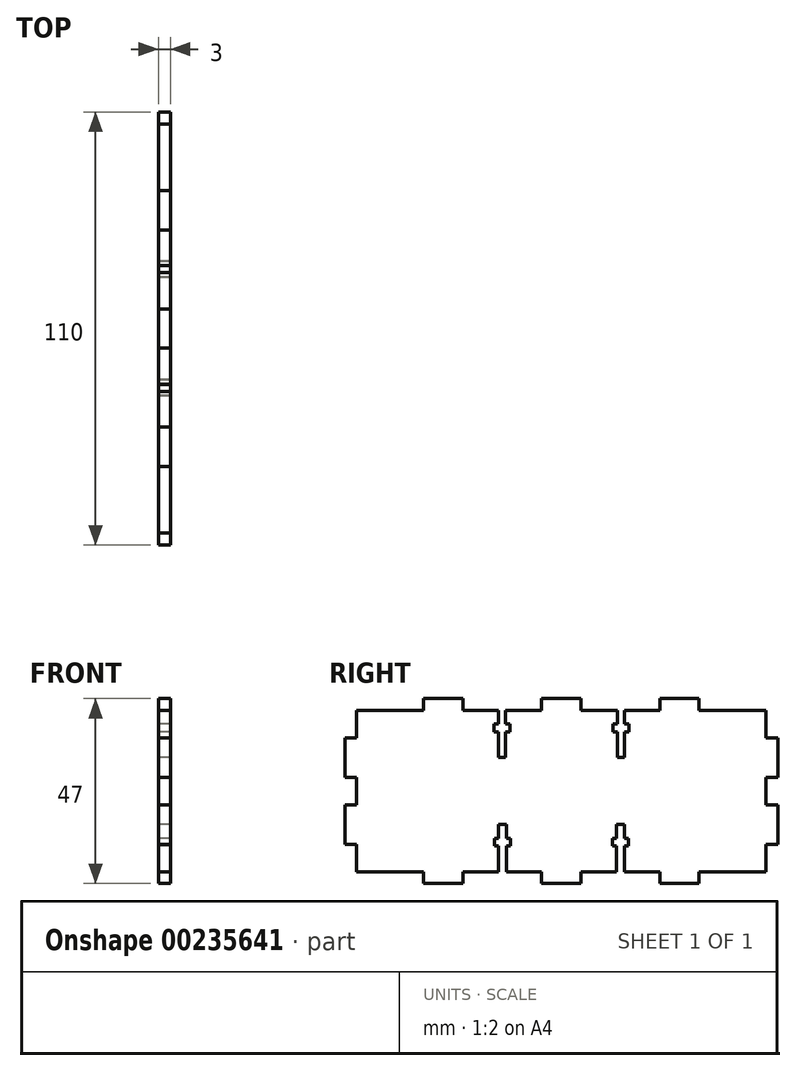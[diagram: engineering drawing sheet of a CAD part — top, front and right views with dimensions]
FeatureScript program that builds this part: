
annotation { "Feature Type Name" : "Feature", "Feature Type Description" : "" }
export const myFeature = defineFeature(function(context is Context, id is Id, definition is map)
    precondition{}
    {
        {
            var Q0;
            Q0=qCreatedBy(makeId("Right.planeOp"),FACE);
            var sketch = newSketch(context, id + "F0", { "sketchPlane" : qUnion([Q0])});
            skLineSegment(sketch, "E0", {"start": v(50.59, -20.79) * mm, "end": v(50.59, -13.79) * mm});
            skLineSegment(sketch, "E1", {"start": v(50.59, -13.79) * mm, "end": v(53.59, -13.79) * mm});
            skLineSegment(sketch, "E2", {"start": v(53.59, -13.79) * mm, "end": v(53.59, -3.79) * mm});
            skLineSegment(sketch, "E3", {"start": v(53.59, -3.79) * mm, "end": v(50.59, -3.79) * mm});
            skLineSegment(sketch, "E4", {"start": v(50.59, -3.79) * mm, "end": v(50.59, 3.21) * mm});
            skLineSegment(sketch, "E5", {"start": v(50.59, 3.21) * mm, "end": v(53.59, 3.21) * mm});
            skLineSegment(sketch, "E6", {"start": v(53.59, 3.21) * mm, "end": v(53.59, 13.21) * mm});
            skLineSegment(sketch, "E7", {"start": v(53.59, 13.21) * mm, "end": v(50.59, 13.21) * mm});
            skLineSegment(sketch, "E8", {"start": v(50.59, 13.21) * mm, "end": v(50.59, 20.21) * mm});
            skLineSegment(sketch, "E9", {"start": v(50.59, 20.21) * mm, "end": v(33.59, 20.21) * mm});
            skLineSegment(sketch, "E10", {"start": v(33.59, 20.21) * mm, "end": v(33.59, 23.21) * mm});
            skLineSegment(sketch, "E11", {"start": v(23.59, 23.21) * mm, "end": v(23.59, 20.21) * mm});
            skLineSegment(sketch, "E12", {"start": v(3.59, 20.21) * mm, "end": v(3.59, 23.21) * mm});
            skLineSegment(sketch, "E13", {"start": v(50.59, -20.79) * mm, "end": v(33.59, -20.79) * mm});
            skLineSegment(sketch, "E14", {"start": v(33.59, -20.79) * mm, "end": v(33.59, -23.79) * mm});
            skLineSegment(sketch, "E15", {"start": v(23.59, -23.79) * mm, "end": v(23.59, -20.79) * mm});
            skLineSegment(sketch, "E16", {"start": v(23.59, -20.79) * mm, "end": v(14.59, -20.79) * mm});
            skLineSegment(sketch, "E17", {"start": v(3.59, -20.79) * mm, "end": v(3.59, -23.79) * mm});
            skLineSegment(sketch, "E18.MirrorCS", {"start": v(-6.41, 20.21) * mm, "end": v(-6.41, 23.21) * mm});
            skLineSegment(sketch, "E19.MirrorCS", {"start": v(-53.41, -13.79) * mm, "end": v(-56.41, -13.79) * mm});
            skLineSegment(sketch, "E20.MirrorCS", {"start": v(-36.41, -20.79) * mm, "end": v(-36.41, -23.79) * mm});
            skLineSegment(sketch, "E21.MirrorCS", {"start": v(-56.41, -3.79) * mm, "end": v(-53.41, -3.79) * mm});
            skLineSegment(sketch, "E22.MirrorCS", {"start": v(-26.41, -23.79) * mm, "end": v(-26.41, -20.79) * mm});
            skLineSegment(sketch, "E23.MirrorCS", {"start": v(-53.41, 3.21) * mm, "end": v(-56.41, 3.21) * mm});
            skLineSegment(sketch, "E24.MirrorCS", {"start": v(-56.41, 13.21) * mm, "end": v(-53.41, 13.21) * mm});
            skLineSegment(sketch, "E25.MirrorCS", {"start": v(-36.41, 20.21) * mm, "end": v(-36.41, 23.21) * mm});
            skLineSegment(sketch, "E26.MirrorCS", {"start": v(-26.41, 23.21) * mm, "end": v(-26.41, 20.21) * mm});
            skLineSegment(sketch, "E27.MirrorCS", {"start": v(-6.41, -20.79) * mm, "end": v(-6.41, -23.79) * mm});
            skLineSegment(sketch, "E28.MirrorCS", {"start": v(-53.41, -20.79) * mm, "end": v(-36.41, -20.79) * mm});
            skLineSegment(sketch, "E29.MirrorCS", {"start": v(-53.41, -20.79) * mm, "end": v(-53.41, -13.79) * mm});
            skLineSegment(sketch, "E30.MirrorCS", {"start": v(-26.41, 20.21) * mm, "end": v(-17.41, 20.21) * mm});
            skLineSegment(sketch, "E31.MirrorCS", {"start": v(-56.41, -13.79) * mm, "end": v(-56.41, -3.79) * mm});
            skLineSegment(sketch, "E32.MirrorCS", {"start": v(-36.41, -23.79) * mm, "end": v(-26.41, -23.79) * mm});
            skLineSegment(sketch, "E33.MirrorCS", {"start": v(-26.41, -20.79) * mm, "end": v(-17.41, -20.79) * mm});
            skLineSegment(sketch, "E34.MirrorCS", {"start": v(-53.41, -3.79) * mm, "end": v(-53.41, 3.21) * mm});
            skLineSegment(sketch, "E35.MirrorCS", {"start": v(-56.41, 3.21) * mm, "end": v(-56.41, 13.21) * mm});
            skLineSegment(sketch, "E36.MirrorCS", {"start": v(-53.41, 13.21) * mm, "end": v(-53.41, 20.21) * mm});
            skLineSegment(sketch, "E37.MirrorCS", {"start": v(-53.41, 20.21) * mm, "end": v(-36.41, 20.21) * mm});
            skLineSegment(sketch, "E38.MirrorCS", {"start": v(-36.41, 23.21) * mm, "end": v(-26.41, 23.21) * mm});
            skPoint(sketch, "E39.centerSnap0", {"position": v(50.59, -0.29) * mm});
            skPoint(sketch, "E39.centerSnap1", {"position": v(42.09, -20.79) * mm});
            skLineSegment(sketch, "E40.top", {"start": v(-17.41, 8.21) * mm, "end": v(-15.63, 8.21) * mm});
            skLineSegment(sketch, "E41", {"start": v(-6.41, -23.79) * mm, "end": v(3.59, -23.79) * mm});
            skLineSegment(sketch, "E42", {"start": v(33.59, -23.79) * mm, "end": v(23.59, -23.79) * mm});
            skLineSegment(sketch, "E43", {"start": v(-6.41, 23.21) * mm, "end": v(3.59, 23.21) * mm});
            skLineSegment(sketch, "E44.trimOffspring", {"start": v(-15.63, 20.21) * mm, "end": v(-6.41, 20.21) * mm});
            skLineSegment(sketch, "E45.MirrorCS", {"start": v(-18.41, -12.29) * mm, "end": v(-17.41, -12.29) * mm});
            skLineSegment(sketch, "E46.MirrorCS", {"start": v(-18.41, -14.29) * mm, "end": v(-17.41, -14.29) * mm});
            skLineSegment(sketch, "E47.MirrorCS", {"start": v(-14.41, -14.29) * mm, "end": v(-14.41, -12.29) * mm});
            skLineSegment(sketch, "E48.MirrorCS", {"start": v(-15.41, -12.29) * mm, "end": v(-14.41, -12.29) * mm});
            skLineSegment(sketch, "E49.MirrorCS", {"start": v(-17.41, -8.79) * mm, "end": v(-15.41, -8.79) * mm});
            skLineSegment(sketch, "E50.MirrorCS", {"start": v(-15.41, -14.29) * mm, "end": v(-14.41, -14.29) * mm});
            skLineSegment(sketch, "E51.MirrorCS", {"start": v(-15.41, -12.29) * mm, "end": v(-15.41, -8.79) * mm});
            skLineSegment(sketch, "E52.MirrorCS", {"start": v(-17.41, -12.29) * mm, "end": v(-17.41, -8.79) * mm});
            skLineSegment(sketch, "E53.MirrorCS", {"start": v(-17.41, -20.79) * mm, "end": v(-17.41, -14.29) * mm});
            skLineSegment(sketch, "E54.MirrorCS", {"start": v(-15.41, -20.79) * mm, "end": v(-15.41, -14.29) * mm});
            skLineSegment(sketch, "E55", {"start": v(23.59, 23.21) * mm, "end": v(33.59, 23.21) * mm});
            skLineSegment(sketch, "E56.MirrorCS", {"start": v(11.59, -14.29) * mm, "end": v(11.59, -12.29) * mm});
            skLineSegment(sketch, "E57.MirrorCS", {"start": v(12.59, -14.29) * mm, "end": v(11.59, -14.29) * mm});
            skLineSegment(sketch, "E58.MirrorCS", {"start": v(15.59, -14.29) * mm, "end": v(14.59, -14.29) * mm});
            skLineSegment(sketch, "E59.MirrorCS", {"start": v(12.59, -12.29) * mm, "end": v(11.59, -12.29) * mm});
            skLineSegment(sketch, "E60.MirrorCS", {"start": v(14.59, -8.79) * mm, "end": v(12.59, -8.79) * mm});
            skLineSegment(sketch, "E61.MirrorCS", {"start": v(15.59, -12.29) * mm, "end": v(14.59, -12.29) * mm});
            skLineSegment(sketch, "E62.MirrorCS", {"start": v(12.59, -12.29) * mm, "end": v(12.59, -8.79) * mm});
            skLineSegment(sketch, "E63.MirrorCS", {"start": v(14.59, -12.29) * mm, "end": v(14.59, -8.79) * mm});
            skLineSegment(sketch, "E64.MirrorCS", {"start": v(14.59, -20.79) * mm, "end": v(14.59, -14.29) * mm});
            skLineSegment(sketch, "E65.MirrorCS", {"start": v(12.59, -20.79) * mm, "end": v(12.59, -14.29) * mm});
            skLineSegment(sketch, "E66.trimOffspring", {"start": v(-15.41, -20.79) * mm, "end": v(-6.41, -20.79) * mm});
            skLineSegment(sketch, "E67.trimOffspring", {"start": v(12.59, -20.79) * mm, "end": v(3.59, -20.79) * mm});
            skLineSegment(sketch, "E68", {"start": v(-17.41, 20.21) * mm, "end": v(-17.41, 16.71) * mm});
            skLineSegment(sketch, "E69", {"start": v(-15.63, 20.21) * mm, "end": v(-15.63, 16.71) * mm});
            skLineSegment(sketch, "E70.bottom", {"start": v(-18.52, 16.71) * mm, "end": v(-17.41, 16.71) * mm});
            skLineSegment(sketch, "E70.top", {"start": v(-18.52, 14.71) * mm, "end": v(-17.41, 14.71) * mm});
            skLineSegment(sketch, "E70.left", {"start": v(-18.52, 16.71) * mm, "end": v(-18.52, 14.71) * mm});
            skLineSegment(sketch, "E70.right", {"start": v(-14.52, 16.71) * mm, "end": v(-14.52, 14.71) * mm});
            skLineSegment(sketch, "E71.trimOffspring", {"start": v(-17.41, 14.71) * mm, "end": v(-17.41, 8.21) * mm});
            skLineSegment(sketch, "E72.trimOffspring", {"start": v(-15.63, 14.71) * mm, "end": v(-15.63, 8.21) * mm});
            skLineSegment(sketch, "E73.trimOffspring", {"start": v(-15.63, 14.71) * mm, "end": v(-14.52, 14.71) * mm});
            skLineSegment(sketch, "E74.trimOffspring", {"start": v(-15.63, 16.71) * mm, "end": v(-14.52, 16.71) * mm});
            skLineSegment(sketch, "E75.MirrorCS", {"start": v(15.7, 14.71) * mm, "end": v(14.59, 14.71) * mm});
            skLineSegment(sketch, "E76.MirrorCS", {"start": v(15.7, 16.71) * mm, "end": v(14.59, 16.71) * mm});
            skLineSegment(sketch, "E77.MirrorCS", {"start": v(12.8, 16.71) * mm, "end": v(11.7, 16.71) * mm});
            skLineSegment(sketch, "E78.MirrorCS", {"start": v(12.8, 14.71) * mm, "end": v(11.7, 14.71) * mm});
            skLineSegment(sketch, "E79.MirrorCS", {"start": v(14.59, 8.21) * mm, "end": v(12.8, 8.21) * mm});
            skLineSegment(sketch, "E80.MirrorCS", {"start": v(14.59, 14.71) * mm, "end": v(14.59, 8.21) * mm});
            skLineSegment(sketch, "E81.MirrorCS", {"start": v(11.7, 16.71) * mm, "end": v(11.7, 14.71) * mm});
            skLineSegment(sketch, "E82.MirrorCS", {"start": v(12.8, 14.71) * mm, "end": v(12.8, 8.21) * mm});
            skLineSegment(sketch, "E83.MirrorCS", {"start": v(15.7, 16.71) * mm, "end": v(15.7, 14.71) * mm});
            skLineSegment(sketch, "E84.MirrorCS", {"start": v(14.59, 20.21) * mm, "end": v(14.59, 16.71) * mm});
            skLineSegment(sketch, "E85", {"start": v(15.59, -14.29) * mm, "end": v(15.59, -12.29) * mm});
            skLineSegment(sketch, "E86", {"start": v(-18.41, -12.29) * mm, "end": v(-18.41, -14.29) * mm});
            skLineSegment(sketch, "E87", {"start": v(12.8, 16.71) * mm, "end": v(12.8, 20.13) * mm});
            skLineSegment(sketch, "E88", {"start": v(23.59, 20.21) * mm, "end": v(14.59, 20.21) * mm});
            skLineSegment(sketch, "E89", {"start": v(3.59, 20.21) * mm, "end": v(12.8, 20.13) * mm});
            skSolve(sketch);
        }
        {
            var Q0;
            Q0=makeQuery(id+"F0.imprint","IMPRINT",FACE,{"disambiguationData":[TD([[makeQuery(id+"F0.imprint","IMPRINT",EDGE,{"derivedFrom":sQuery(id+"F0.wireOp",EDGE,"E0")}),1.0]])]});
            extrude(context, id + "F1", {"entities" : qUnion([Q0]), "depth" : 3 * mm});
        }
    });
